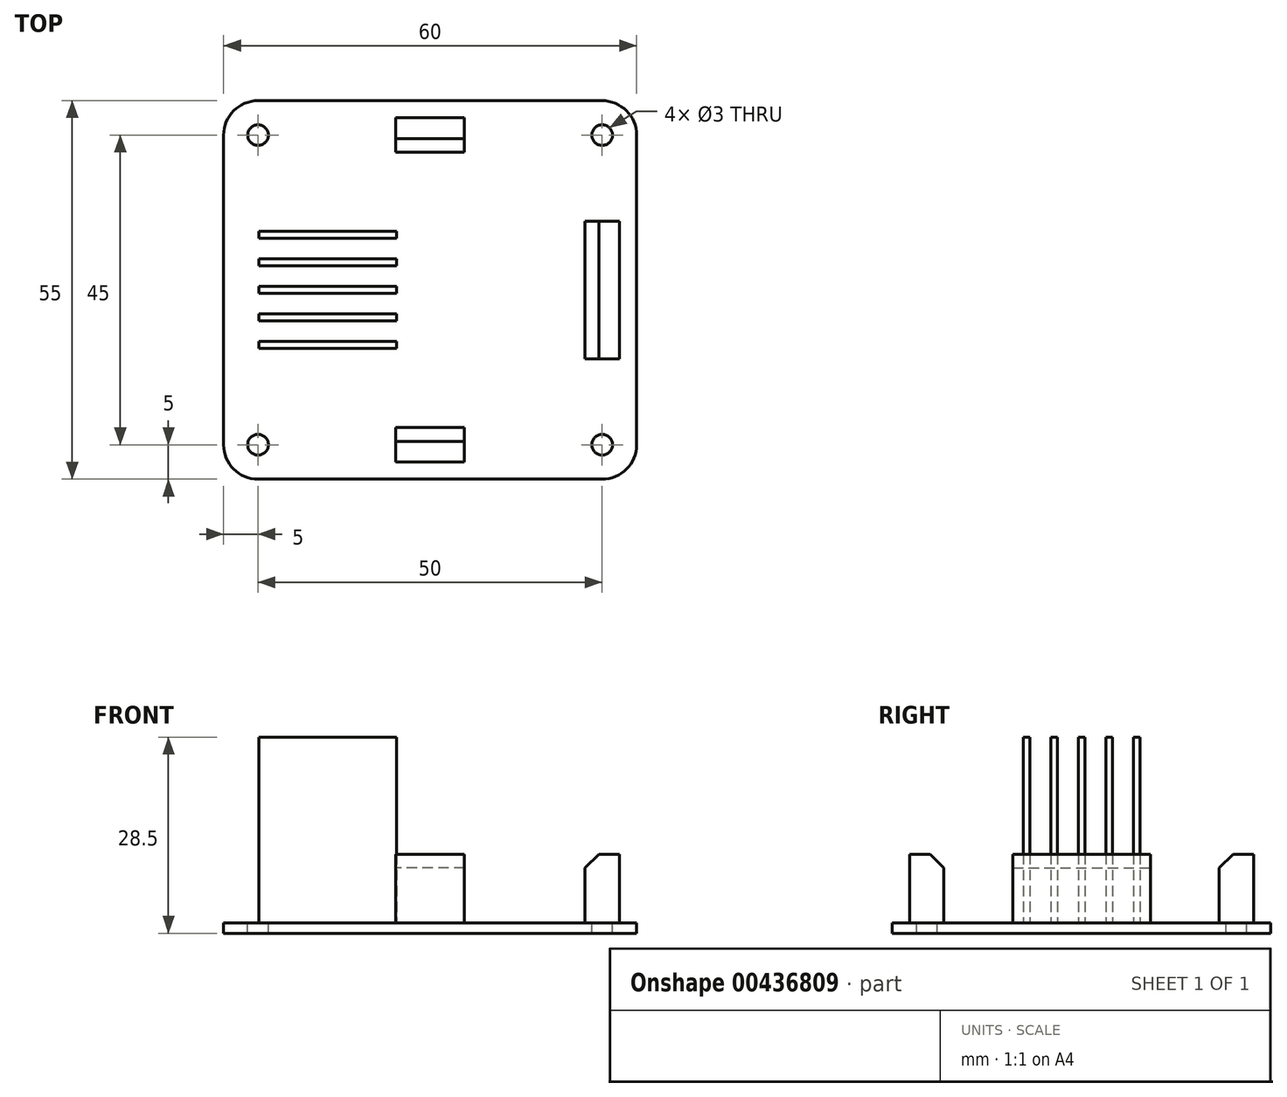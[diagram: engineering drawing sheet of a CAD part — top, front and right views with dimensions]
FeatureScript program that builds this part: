
annotation { "Feature Type Name" : "Feature", "Feature Type Description" : "" }
export const myFeature = defineFeature(function(context is Context, id is Id, definition is map)
    precondition{}
    {
        {
            var Q0;
            Q0=qCreatedBy(makeId("Top.planeOp"),FACE);
            var sketch = newSketch(context, id + "F0", { "sketchPlane" : qUnion([Q0])});
            skLineSegment(sketch, "E0.bottom", {"start": v(25, 27.5) * mm, "end": v(-25, 27.5) * mm});
            skLineSegment(sketch, "E0.top", {"start": v(25, -27.5) * mm, "end": v(-25, -27.5) * mm});
            skLineSegment(sketch, "E0.left", {"start": v(30, 22.5) * mm, "end": v(30, -22.5) * mm});
            skLineSegment(sketch, "E0.right", {"start": v(-30, 22.5) * mm, "end": v(-30, -22.5) * mm});
            skPoint(sketch, "E0.middle", {"position": v(0, 0) * mm});
            skPoint(sketch, "E1.visualSharp", {"position": v(-30, 27.5) * mm});
            skArc(sketch, "E1.filletArc", {"start": v(-25, 27.5) * mm, "mid": v(-28.54, 26.04) * mm, "end": v(-30, 22.5) * mm});
            skPoint(sketch, "E2.visualSharp", {"position": v(30, 27.5) * mm});
            skArc(sketch, "E2.filletArc", {"start": v(30, 22.5) * mm, "mid": v(28.54, 26.04) * mm, "end": v(25, 27.5) * mm});
            skPoint(sketch, "E3.visualSharp", {"position": v(30, -27.5) * mm});
            skArc(sketch, "E3.filletArc", {"start": v(25, -27.5) * mm, "mid": v(28.54, -26.04) * mm, "end": v(30, -22.5) * mm});
            skPoint(sketch, "E4.visualSharp", {"position": v(-30, -27.5) * mm});
            skArc(sketch, "E4.filletArc", {"start": v(-30, -22.5) * mm, "mid": v(-28.54, -26.04) * mm, "end": v(-25, -27.5) * mm});
            skCircle(sketch, "E5", {"center": v(25, 22.5) * mm, "radius": 1.5 * mm});
            skCircle(sketch, "E6", {"center": v(-25, 22.5) * mm, "radius": 1.5 * mm});
            skCircle(sketch, "E7", {"center": v(-25, -22.5) * mm, "radius": 1.5 * mm});
            skCircle(sketch, "E8", {"center": v(25, -22.5) * mm, "radius": 1.5 * mm});
            skSolve(sketch);
        }
        {
            var Q0;
            Q0 = qSketchRegion(id + "F0", true);
            extrude(context, id + "F1", {"entities" : qUnion([Q0]), "oppositeDirection" : true, "depth" : 1.5 * mm});
        }
        {
            var Q0;
            Q0=makeQuery(id+"F1.opExtrude","CAP_FACE",FACE,{"disambiguationData":[OSD([sQuery(id+"F0.wireOp",EDGE,"E0.bottom"),sQuery(id+"F0.wireOp",EDGE,"E0.top"),sQuery(id+"F0.wireOp",EDGE,"E0.left"),sQuery(id+"F0.wireOp",EDGE,"E0.right"),sQuery(id+"F0.wireOp",EDGE,"E1.filletArc"),sQuery(id+"F0.wireOp",EDGE,"E2.filletArc"),sQuery(id+"F0.wireOp",EDGE,"E3.filletArc"),sQuery(id+"F0.wireOp",EDGE,"E4.filletArc"),sQuery(id+"F0.wireOp",EDGE,"E5"),sQuery(id+"F0.wireOp",EDGE,"E6"),sQuery(id+"F0.wireOp",EDGE,"E7"),sQuery(id+"F0.wireOp",EDGE,"E8")])],"isStart":true});
            var sketch = newSketch(context, id + "F2", { "sketchPlane" : qUnion([Q0])});
            skLineSegment(sketch, "E9.bottom", {"start": v(-24.88, 0.5) * mm, "end": v(-4.88, 0.5) * mm});
            skLineSegment(sketch, "E9.top", {"start": v(-24.88, -0.5) * mm, "end": v(-4.88, -0.5) * mm});
            skLineSegment(sketch, "E9.left", {"start": v(-24.88, 0.5) * mm, "end": v(-24.88, -0.5) * mm});
            skLineSegment(sketch, "E9.right", {"start": v(-4.88, 0.5) * mm, "end": v(-4.88, -0.5) * mm});
            skLineSegment(sketch, "E10.bottom", {"start": v(-24.88, 4.5) * mm, "end": v(-4.88, 4.5) * mm});
            skLineSegment(sketch, "E10.top", {"start": v(-24.88, 3.5) * mm, "end": v(-4.88, 3.5) * mm});
            skLineSegment(sketch, "E10.left", {"start": v(-24.88, 4.5) * mm, "end": v(-24.88, 3.5) * mm});
            skLineSegment(sketch, "E10.right", {"start": v(-4.88, 4.5) * mm, "end": v(-4.88, 3.5) * mm});
            skLineSegment(sketch, "E11.bottom", {"start": v(-24.88, 8.5) * mm, "end": v(-4.88, 8.5) * mm});
            skLineSegment(sketch, "E11.top", {"start": v(-24.88, 7.5) * mm, "end": v(-4.88, 7.5) * mm});
            skLineSegment(sketch, "E11.left", {"start": v(-24.88, 8.5) * mm, "end": v(-24.88, 7.5) * mm});
            skLineSegment(sketch, "E11.right", {"start": v(-4.88, 8.5) * mm, "end": v(-4.88, 7.5) * mm});
            skLineSegment(sketch, "E12.MirrorCS", {"start": v(-24.88, -4.5) * mm, "end": v(-24.88, -3.5) * mm});
            skLineSegment(sketch, "E13.MirrorCS", {"start": v(-24.88, -8.5) * mm, "end": v(-24.88, -7.5) * mm});
            skLineSegment(sketch, "E14.MirrorCS", {"start": v(-4.88, -8.5) * mm, "end": v(-4.88, -7.5) * mm});
            skLineSegment(sketch, "E15.MirrorCS", {"start": v(-4.88, -4.5) * mm, "end": v(-4.88, -3.5) * mm});
            skLineSegment(sketch, "E16.MirrorCS", {"start": v(-24.88, -8.5) * mm, "end": v(-4.88, -8.5) * mm});
            skLineSegment(sketch, "E17.MirrorCS", {"start": v(-24.88, -7.5) * mm, "end": v(-4.88, -7.5) * mm});
            skLineSegment(sketch, "E18.MirrorCS", {"start": v(-24.88, -4.5) * mm, "end": v(-4.88, -4.5) * mm});
            skLineSegment(sketch, "E19.MirrorCS", {"start": v(-24.88, -3.5) * mm, "end": v(-4.88, -3.5) * mm});
            skSolve(sketch);
        }
        {
            var Q0;
            Q0 = qSketchRegion(id + "F2", true);
            extrude(context, id + "F3", {"entities" : qUnion([Q0]), "operationType" : NewBodyOperationType.ADD, "depth" : 27 * mm});
        }
        {
            var Q0;
            Q0=makeQuery(id+"F1.opExtrude","CAP_FACE",FACE,{"disambiguationData":[OSD([sQuery(id+"F0.wireOp",EDGE,"E0.bottom"),sQuery(id+"F0.wireOp",EDGE,"E0.top"),sQuery(id+"F0.wireOp",EDGE,"E0.left"),sQuery(id+"F0.wireOp",EDGE,"E0.right"),sQuery(id+"F0.wireOp",EDGE,"E1.filletArc"),sQuery(id+"F0.wireOp",EDGE,"E2.filletArc"),sQuery(id+"F0.wireOp",EDGE,"E3.filletArc"),sQuery(id+"F0.wireOp",EDGE,"E4.filletArc"),sQuery(id+"F0.wireOp",EDGE,"E5"),sQuery(id+"F0.wireOp",EDGE,"E6"),sQuery(id+"F0.wireOp",EDGE,"E7"),sQuery(id+"F0.wireOp",EDGE,"E8")])],"isStart":true});
            var sketch = newSketch(context, id + "F4", { "sketchPlane" : qUnion([Q0])});
            skPoint(sketch, "E20.middle", {"position": v(0, 27.5) * mm});
            skLineSegment(sketch, "E21.bottom", {"start": v(5, 20) * mm, "end": v(-5, 20) * mm});
            skLineSegment(sketch, "E21.top", {"start": v(5, 25) * mm, "end": v(-5, 25) * mm});
            skLineSegment(sketch, "E21.left", {"start": v(5, 20) * mm, "end": v(5, 25) * mm});
            skLineSegment(sketch, "E21.right", {"start": v(-5, 20) * mm, "end": v(-5, 25) * mm});
            skPoint(sketch, "E21.middle", {"position": v(0, 22.5) * mm});
            skLineSegment(sketch, "E22.MirrorCS", {"start": v(5, -25) * mm, "end": v(-5, -25) * mm});
            skPoint(sketch, "E23.MirrorP", {"position": v(0, -27.5) * mm});
            skLineSegment(sketch, "E24.MirrorCS", {"start": v(-5, -20) * mm, "end": v(-5, -25) * mm});
            skLineSegment(sketch, "E25.MirrorCS", {"start": v(5, -20) * mm, "end": v(-5, -20) * mm});
            skLineSegment(sketch, "E26.MirrorCS", {"start": v(5, -20) * mm, "end": v(5, -25) * mm});
            skPoint(sketch, "E27.MirrorP", {"position": v(0, -22.5) * mm});
            skPoint(sketch, "E28.endSnap0", {"position": v(30, 0) * mm});
            skLineSegment(sketch, "E29.bottom", {"start": v(22.5, 10) * mm, "end": v(27.5, 10) * mm});
            skLineSegment(sketch, "E29.top", {"start": v(22.5, -10) * mm, "end": v(27.5, -10) * mm});
            skLineSegment(sketch, "E29.left", {"start": v(22.5, 10) * mm, "end": v(22.5, -10) * mm});
            skLineSegment(sketch, "E29.right", {"start": v(27.5, 10) * mm, "end": v(27.5, -10) * mm});
            skPoint(sketch, "E29.middle", {"position": v(25, 0) * mm});
            skSolve(sketch);
        }
        {
            var Q0;
            Q0 = qSketchRegion(id + "F4", true);
            extrude(context, id + "F5", {"entities" : qUnion([Q0]), "operationType" : NewBodyOperationType.ADD, "depth" : 10 * mm});
        }
        {
            var Q0;
            Q0=makeQuery(id+"F5.opExtrude","CAP_EDGE",EDGE,{"disambiguationData":[OSD([sQuery(id+"F4.wireOp",EDGE,"E21.bottom")])],"isStart":false});
            var Q1;
            Q1=makeQuery(id+"F5.opExtrude","CAP_EDGE",EDGE,{"disambiguationData":[OSD([sQuery(id+"F4.wireOp",EDGE,"E29.left")])],"isStart":false});
            var Q2;
            Q2=makeQuery(id+"F5.opExtrude","CAP_EDGE",EDGE,{"disambiguationData":[OSD([sQuery(id+"F4.wireOp",EDGE,"E25.MirrorCS")])],"isStart":false});
            chamfer(context, id + "F6", {"entities" : qUnion([Q0, Q1, Q2]), "width" : 2 * mm, "tangentPropagation" : true});
        }
    });
